# Revit family: Panel_Leviton_Outdoor_30Pos
name_source: partatom
category: Electrical Equipment
units: mm (PartAtom-declared; Revit-internal decimal feet)

## family parameters
Always vertical = Yes
Classification Number = 23.80.30.11.17
Cut with Voids When Loaded = No
Maintain Annotation Orientation = No
Panel Configuration = Two Columns, Circuits Across
Part Type = Panelboard
Room Calculation Point = No
Round Connector Dimension = Use Diameter
Shared = No
Work Plane-Based = No

## types (6) — shared parameters
Body = Galvanized Steel_Gray Baked Enamel
Neutral Rating = 100.00%
Voltage Comments = 208
Voltage_MEP = 208 V
zero-valued in all types: Default Elevation, Unit Depth, Unit Height, Unit Width

## per-type parameters (varying)
| type | Description | Mains Type | Model |
| LP315-3B - 240V / 150A | Outdoor Load Center; NEMA 3R with Main Breaker; 150A 30 Spaces; 22KA Interrupt Rating; Enclosure and Door Only. | Main Breaker | LP315-3B |
| LP320-3B - 240V / 200A | Outdoor Load Center; NEMA 3R with Main Breaker; 200A 30 Spaces; 22KA Interrupt Rating; Enclosure and Door Only. | Main Breaker | LP320-3B |
| LP320-3L - 240V / 200A | Outdoor Load Center; NEMA 3R with Main Lugs; 200A 30 Spaces; 22KA Interrupt Rating; Enclosure and Door Only. | Main Lug | LP320-3L |
| LP315-3B - 120V / 150A | Outdoor Load Center; NEMA 3R with Main Breaker; 150A 30 Spaces; 22KA Interrupt Rating; Enclosure and Door Only. | Main Breaker | LP315-3B |
| LP320-3B - 120V / 200A | Outdoor Load Center; NEMA 3R with Main Breaker; 200A 30 Spaces; 22KA Interrupt Rating; Enclosure and Door Only. | Main Breaker | LP320-3B |
| LP320-3L - 120V / 200A | Outdoor Load Center; NEMA 3R with Main Lugs; 200A 30 Spaces; 22KA Interrupt Rating; Enclosure and Door Only. | Main Lug | LP320-3L |

## geometry (parser evidence)
native form markers: Sweep x6
no freeform markers — native parametric forms only
